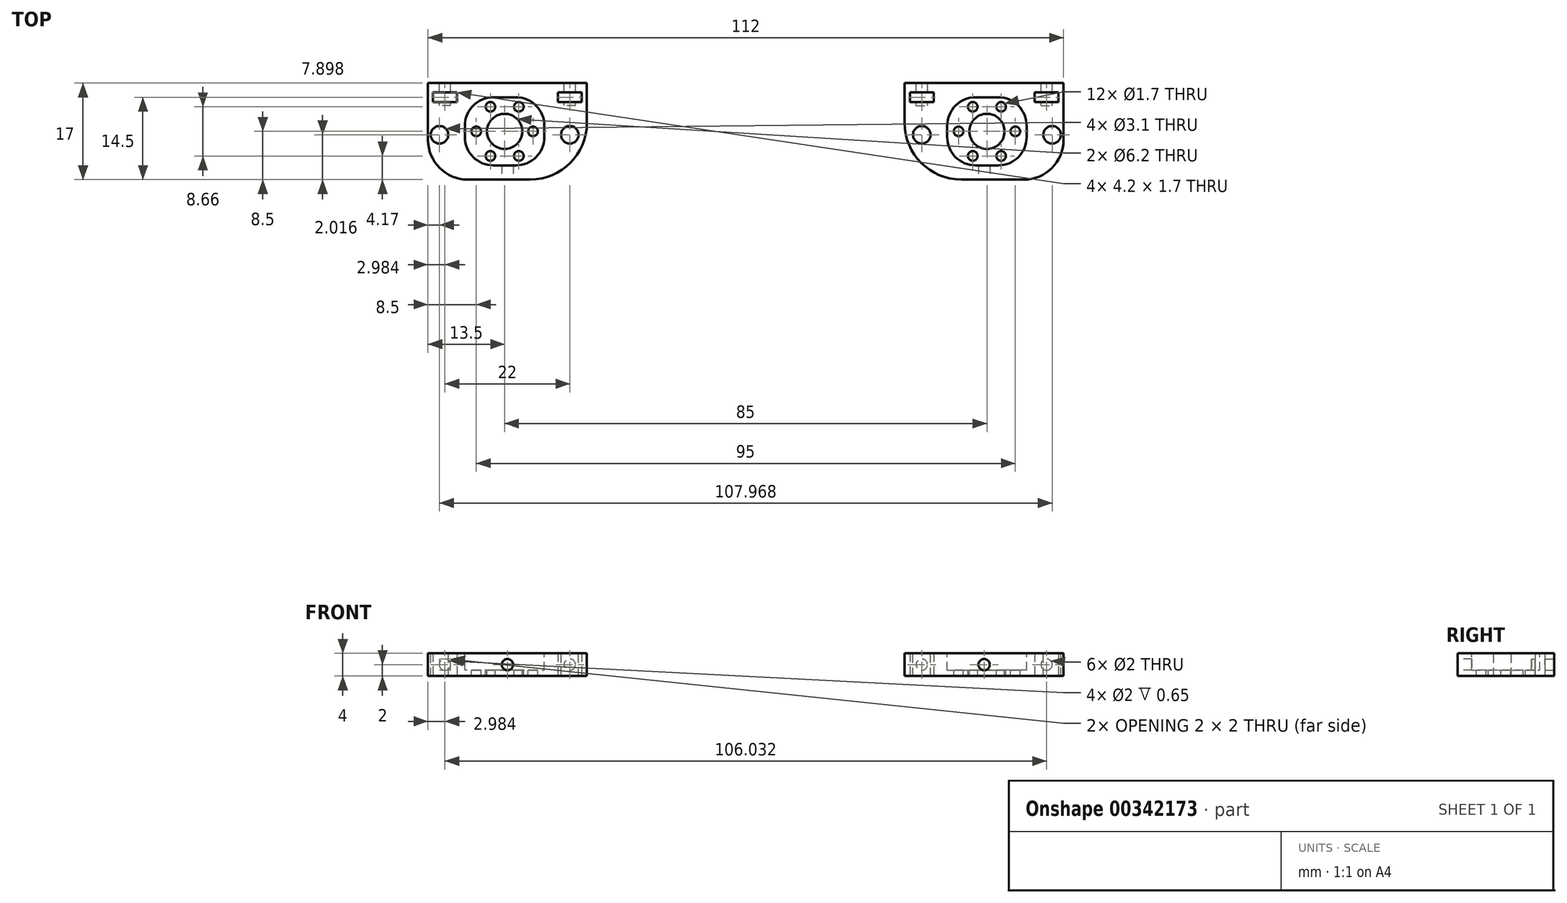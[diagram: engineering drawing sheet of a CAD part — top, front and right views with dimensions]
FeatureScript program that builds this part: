
annotation { "Feature Type Name" : "Feature", "Feature Type Description" : "" }
export const myFeature = defineFeature(function(context is Context, id is Id, definition is map)
    precondition{}
    {
        {
            var Q0;
            Q0=qCreatedBy(makeId("Front.planeOp"),FACE);
            var sketch = newSketch(context, id + "F0", { "sketchPlane" : qUnion([Q0])});
            skLineSegment(sketch, "E0.bottom", {"start": v(0, 0) * mm, "end": v(28, 0) * mm});
            skLineSegment(sketch, "E0.top", {"start": v(0, 17) * mm, "end": v(28, 17) * mm});
            skLineSegment(sketch, "E0.left", {"start": v(0, 0) * mm, "end": v(0, 17) * mm});
            skLineSegment(sketch, "E0.right", {"start": v(28, 0) * mm, "end": v(28, 17) * mm});
            skCircle(sketch, "E1", {"center": v(14.5, 8.5) * mm, "radius": 3.1 * mm});
            skCircle(sketch, "E2", {"center": v(19.5, 8.5) * mm, "radius": 0.85 * mm});
            skCircle(sketch, "E3.1.0", {"center": v(17, 12.83) * mm, "radius": 0.85 * mm});
            skCircle(sketch, "E3.2.0", {"center": v(12, 12.83) * mm, "radius": 0.85 * mm});
            skCircle(sketch, "E3.3.0", {"center": v(9.5, 8.5) * mm, "radius": 0.85 * mm});
            skCircle(sketch, "E3.4.0", {"center": v(12, 4.17) * mm, "radius": 0.85 * mm});
            skCircle(sketch, "E3.5.0", {"center": v(17, 4.17) * mm, "radius": 0.85 * mm});
            skLineSegment(sketch, "E4.bottom", {"start": v(7.5, 14.5) * mm, "end": v(21.5, 14.5) * mm});
            skLineSegment(sketch, "E4.top", {"start": v(7.5, 2.5) * mm, "end": v(21.5, 2.5) * mm});
            skLineSegment(sketch, "E4.left", {"start": v(7.5, 14.5) * mm, "end": v(7.5, 2.5) * mm});
            skLineSegment(sketch, "E4.right", {"start": v(21.5, 14.5) * mm, "end": v(21.5, 2.5) * mm});
            skCircle(sketch, "E5", {"center": v(3.02, 9.1) * mm, "radius": 1.55 * mm});
            skLineSegment(sketch, "E6", {"start": v(3.02, 9.1) * mm, "end": v(14.5, 8.5) * mm});
            skLineSegment(sketch, "E7", {"start": v(14.5, 8.5) * mm, "end": v(0, 8.5) * mm});
            skLineSegment(sketch, "E8", {"start": v(14.5, 8.5) * mm, "end": v(14.5, 11.6) * mm});
            skCircle(sketch, "E9.MirrorC", {"center": v(25.98, 9.1) * mm, "radius": 1.55 * mm});
            skSolve(sketch);
        }
        {
            var Q0;
            Q0=makeQuery(id+"F0.imprint","IMPRINT",FACE,{"disambiguationData":[TD([[makeQuery(id+"F0.imprint","IMPRINT",EDGE,{"derivedFrom":sQuery(id+"F0.wireOp",EDGE,"E0.bottom")}),1.0]])]});
            var Q1;
            Q1=makeQuery(id+"F0.imprint","IMPRINT",FACE,{"disambiguationData":[TD([[makeQuery(id+"F0.imprint","IMPRINT",EDGE,{"derivedFrom":sQuery(id+"F0.wireOp",EDGE,"E1")}),-1.0]])]});
            var Q2;
            Q2=makeQuery(id+"F0.imprint","IMPRINT",FACE,{"disambiguationData":[TD([[makeQuery(id+"F0.imprint","IMPRINT",EDGE,{"derivedFrom":sQuery(id+"F0.wireOp",EDGE,"E2")}),-1.0]])]});
            var Q3;
            {var subQ0=sQuery(id+"F0.wireOp",EDGE,"E6");var subQ1=sQuery(id+"F0.wireOp",EDGE,"E3.3.0");var subQ2=makeQuery(id+"F0.imprint","INTERSECT",VERTEX,{"disambiguationData":[OD(0.0)],"derivedFrom":[subQ1,subQ0]});Q3=makeQuery(id+"F0.imprint","IMPRINT",FACE,{"disambiguationData":[TD([[makeQuery(id+"F0.imprint","IMPRINT",EDGE,{"disambiguationData":[TD([[subQ2,1.0]])],"derivedFrom":subQ1}),-1.0]])]});}
            var Q4;
            {var subQ0=sQuery(id+"F0.wireOp",EDGE,"E7");var subQ1=sQuery(id+"F0.wireOp",EDGE,"E4.left");var subQ2=makeQuery(id+"F0.imprint","INTERSECT",VERTEX,{"derivedFrom":[subQ1,subQ0]});Q4=makeQuery(id+"F0.imprint","IMPRINT",FACE,{"disambiguationData":[TD([[makeQuery(id+"F0.imprint","IMPRINT",EDGE,{"disambiguationData":[TD([[subQ2,-1.0]])],"derivedFrom":subQ1}),-1.0]])]});}
            var Q5;
            {var subQ0=sQuery(id+"F0.wireOp",EDGE,"E6");var subQ1=sQuery(id+"F0.wireOp",EDGE,"E4.left");var subQ2=makeQuery(id+"F0.imprint","INTERSECT",VERTEX,{"derivedFrom":[subQ1,subQ0]});Q5=makeQuery(id+"F0.imprint","IMPRINT",FACE,{"disambiguationData":[TD([[makeQuery(id+"F0.imprint","IMPRINT",EDGE,{"disambiguationData":[TD([[subQ2,-1.0]])],"derivedFrom":subQ1}),-1.0]])]});}
            var Q6;
            {var subQ0=sQuery(id+"F0.wireOp",EDGE,"E6");var subQ1=sQuery(id+"F0.wireOp",EDGE,"E3.3.0");var subQ2=makeQuery(id+"F0.imprint","INTERSECT",VERTEX,{"disambiguationData":[OD(1.0)],"derivedFrom":[subQ1,subQ0]});Q6=makeQuery(id+"F0.imprint","IMPRINT",FACE,{"disambiguationData":[TD([[makeQuery(id+"F0.imprint","IMPRINT",EDGE,{"disambiguationData":[TD([[subQ2,-1.0]])],"derivedFrom":subQ1}),-1.0]])]});}
            extrude(context, id + "F1", {"entities" : qUnion([Q0, Q1, Q2, Q3, Q4, Q5, Q6]), "depth" : 4 * mm});
        }
        {
            var Q0;
            Q0=makeQuery(id+"F1.opExtrude","SWEPT_EDGE",EDGE,{"disambiguationData":[OSD([sQuery(id+"F0.wireOp",EDGE,"E0.top"),sQuery(id+"F0.wireOp",EDGE,"E0.left")])]});
            fillet(context, id + "F2", {"entities" : qUnion([Q0]), "radius" : 10 * mm, "tangentPropagation" : true, "allowEdgeOverflow" : false});
        }
        {
            var Q0;
            Q0=makeQuery(id+"F0.imprint","IMPRINT",FACE,{"disambiguationData":[TD([[makeQuery(id+"F0.imprint","IMPRINT",EDGE,{"derivedFrom":sQuery(id+"F0.wireOp",EDGE,"E2")}),-1.0]])]});
            var Q1;
            {var subQ0=sQuery(id+"F0.wireOp",EDGE,"E6");var subQ1=sQuery(id+"F0.wireOp",EDGE,"E1");var subQ2=makeQuery(id+"F0.imprint","INTERSECT",VERTEX,{"derivedFrom":[subQ1,subQ0]});Q1=makeQuery(id+"F0.imprint","IMPRINT",FACE,{"disambiguationData":[TD([[makeQuery(id+"F0.imprint","IMPRINT",EDGE,{"disambiguationData":[TD([[subQ2,1.0]])],"derivedFrom":subQ1}),-1.0]])]});}
            var Q2;
            {var subQ0=sQuery(id+"F0.wireOp",EDGE,"E6");var subQ1=sQuery(id+"F0.wireOp",EDGE,"E3.3.0");var subQ2=makeQuery(id+"F0.imprint","INTERSECT",VERTEX,{"disambiguationData":[OD(1.0)],"derivedFrom":[subQ1,subQ0]});Q2=makeQuery(id+"F0.imprint","IMPRINT",FACE,{"disambiguationData":[TD([[makeQuery(id+"F0.imprint","IMPRINT",EDGE,{"disambiguationData":[TD([[subQ2,-1.0]])],"derivedFrom":subQ1}),-1.0]])]});}
            var Q3;
            {var subQ0=sQuery(id+"F0.wireOp",EDGE,"E6");var subQ1=sQuery(id+"F0.wireOp",EDGE,"E1");var subQ2=makeQuery(id+"F0.imprint","INTERSECT",VERTEX,{"derivedFrom":[subQ1,subQ0]});Q3=makeQuery(id+"F0.imprint","IMPRINT",FACE,{"disambiguationData":[TD([[makeQuery(id+"F0.imprint","IMPRINT",EDGE,{"disambiguationData":[TD([[subQ2,-1.0]])],"derivedFrom":subQ1}),-1.0]])]});}
            extrude(context, id + "F3", {"entities" : qUnion([Q0, Q1, Q2, Q3]), "operationType" : NewBodyOperationType.REMOVE, "depth" : 3 * mm});
        }
        {
            var Q0;
            Q0=makeQuery(id+"F3.boolean.opBoolean","COPY",EDGE,{"derivedFrom":makeQuery(id+"F3.opExtrude","SWEPT_EDGE",EDGE,{"disambiguationData":[OSD([sQuery(id+"F0.wireOp",EDGE,"E4.bottom"),sQuery(id+"F0.wireOp",EDGE,"E4.right")])]})});
            var Q1;
            Q1=makeQuery(id+"F3.boolean.opBoolean","COPY",EDGE,{"derivedFrom":makeQuery(id+"F3.opExtrude","SWEPT_EDGE",EDGE,{"disambiguationData":[OSD([sQuery(id+"F0.wireOp",EDGE,"E4.top"),sQuery(id+"F0.wireOp",EDGE,"E4.right")])]})});
            var Q2;
            Q2=makeQuery(id+"F3.boolean.opBoolean","COPY",EDGE,{"derivedFrom":makeQuery(id+"F3.opExtrude","SWEPT_EDGE",EDGE,{"disambiguationData":[OSD([sQuery(id+"F0.wireOp",EDGE,"E4.top"),sQuery(id+"F0.wireOp",EDGE,"E4.left")])]})});
            var Q3;
            Q3=makeQuery(id+"F3.boolean.opBoolean","COPY",EDGE,{"derivedFrom":makeQuery(id+"F3.opExtrude","SWEPT_EDGE",EDGE,{"disambiguationData":[OSD([sQuery(id+"F0.wireOp",EDGE,"E4.bottom"),sQuery(id+"F0.wireOp",EDGE,"E4.left")])]})});
            fillet(context, id + "F4", {"entities" : qUnion([Q0, Q1, Q2, Q3]), "radius" : 5 * mm, "tangentPropagation" : true, "allowEdgeOverflow" : false});
        }
        {
            var Q0;
            Q0=makeQuery(id+"F1.opExtrude","SWEPT_EDGE",EDGE,{"disambiguationData":[OSD([sQuery(id+"F0.wireOp",EDGE,"E0.top"),sQuery(id+"F0.wireOp",EDGE,"E0.right")])]});
            fillet(context, id + "F5", {"entities" : qUnion([Q0]), "radius" : 7 * mm, "tangentPropagation" : true, "allowEdgeOverflow" : false});
        }
        {
            var Q0;
            Q0=makeQuery(id+"F1.opExtrude","SWEPT_FACE",FACE,{"disambiguationData":[OSD([sQuery(id+"F0.wireOp",EDGE,"E0.bottom")])]});
            var sketch = newSketch(context, id + "F6", { "sketchPlane" : qUnion([Q0])});
            skCircle(sketch, "E10", {"center": v(3.02, 2) * mm, "radius": 1 * mm});
            skCircle(sketch, "E11", {"center": v(25.02, 2) * mm, "radius": 1 * mm});
            skSolve(sketch);
        }
        {
            var Q0;
            Q0=qSketchRegion(id+"F6",true);
            extrude(context, id + "F7", {"entities" : qUnion([Q0]), "operationType" : NewBodyOperationType.REMOVE, "oppositeDirection" : true, "depth" : 4 * mm});
        }
        {
            var Q0;
            Q0=makeQuery(id+"F1.opExtrude","CAP_FACE",FACE,{"disambiguationData":[OSD([sQuery(id+"F0.wireOp",EDGE,"E0.bottom"),sQuery(id+"F0.wireOp",EDGE,"E0.top"),sQuery(id+"F0.wireOp",EDGE,"E0.left"),sQuery(id+"F0.wireOp",EDGE,"E0.right"),sQuery(id+"F0.wireOp",EDGE,"wE7doQa1-f1d0-D7SE-Vx9v-5G1ykLdNQw0D"),sQuery(id+"F0.wireOp",EDGE,"E1"),sQuery(id+"F0.wireOp",EDGE,"E2"),sQuery(id+"F0.wireOp",EDGE,"E3.1.0"),sQuery(id+"F0.wireOp",EDGE,"E3.2.0"),sQuery(id+"F0.wireOp",EDGE,"E3.3.0"),sQuery(id+"F0.wireOp",EDGE,"E3.4.0"),sQuery(id+"F0.wireOp",EDGE,"E3.5.0")])],"isStart":false});
            var sketch = newSketch(context, id + "F8", { "sketchPlane" : qUnion([Q0])});
            skLineSegment(sketch, "E12.bottom", {"start": v(0.92, 3.35) * mm, "end": v(5.12, 3.35) * mm});
            skLineSegment(sketch, "E12.top", {"start": v(0.92, 1.65) * mm, "end": v(5.12, 1.65) * mm});
            skLineSegment(sketch, "E12.left", {"start": v(0.92, 3.35) * mm, "end": v(0.92, 1.65) * mm});
            skLineSegment(sketch, "E12.right", {"start": v(5.12, 3.35) * mm, "end": v(5.12, 1.65) * mm});
            skPoint(sketch, "E12.middle", {"position": v(3.02, 2.5) * mm});
            skLineSegment(sketch, "E13.bottom", {"start": v(27.12, 3.35) * mm, "end": v(22.92, 3.35) * mm});
            skLineSegment(sketch, "E13.top", {"start": v(27.12, 1.65) * mm, "end": v(22.92, 1.65) * mm});
            skLineSegment(sketch, "E13.left", {"start": v(27.12, 3.35) * mm, "end": v(27.12, 1.65) * mm});
            skLineSegment(sketch, "E13.right", {"start": v(22.92, 3.35) * mm, "end": v(22.92, 1.65) * mm});
            skPoint(sketch, "E13.middle", {"position": v(25.02, 2.5) * mm});
            skSolve(sketch);
        }
        {
            var Q0;
            Q0=qSketchRegion(id+"F8",true);
            extrude(context, id + "F9", {"entities" : qUnion([Q0]), "operationType" : NewBodyOperationType.REMOVE, "oppositeDirection" : true, "depth" : 4 * mm});
        }
        {
            var Q0;
            Q0=makeQuery(id+"F1.opExtrude","SWEPT_FACE",FACE,{"disambiguationData":[OSD([sQuery(id+"F0.wireOp",EDGE,"E0.top")])]});
            var sketch = newSketch(context, id + "F10", { "sketchPlane" : qUnion([Q0])});
            skPoint(sketch, "E14", {"position": v(15.5, -4) * mm});
            skPoint(sketch, "E15.positionSnap0", {"position": v(10, -2) * mm});
            skPoint(sketch, "E16", {"position": v(0, -2) * mm});
            skPoint(sketch, "E17", {"position": v(14, -2) * mm});
            skCircle(sketch, "E18", {"center": v(14, -2) * mm, "radius": 1 * mm});
            skSolve(sketch);
        }
        {
            var Q0;
            Q0=makeQuery(id+"F10.imprint","IMPRINT",FACE,{"disambiguationData":[TD([[makeQuery(id+"F10.imprint","IMPRINT",EDGE,{"derivedFrom":sQuery(id+"F10.wireOp",EDGE,"E18")}),1.0]])]});
            extrude(context, id + "F11", {"entities" : qUnion([Q0]), "operationType" : NewBodyOperationType.REMOVE, "oppositeDirection" : true, "depth" : 8 * mm});
        }
        {
            var Q0;
            Q0=makeQuery(id+"F1.opExtrude","SWEPT_BODY",BODY,{"disambiguationData":[OSD([sQuery(id+"F0.wireOp",EDGE,"E0.bottom"),sQuery(id+"F0.wireOp",EDGE,"E0.top"),sQuery(id+"F0.wireOp",EDGE,"E0.left"),sQuery(id+"F0.wireOp",EDGE,"E0.right"),sQuery(id+"F0.wireOp",EDGE,"E1"),sQuery(id+"F0.wireOp",EDGE,"E2"),sQuery(id+"F0.wireOp",EDGE,"E3.1.0"),sQuery(id+"F0.wireOp",EDGE,"E3.2.0"),sQuery(id+"F0.wireOp",EDGE,"E3.3.0"),sQuery(id+"F0.wireOp",EDGE,"E3.4.0"),sQuery(id+"F0.wireOp",EDGE,"E3.5.0"),sQuery(id+"F0.wireOp",EDGE,"E5"),sQuery(id+"F0.wireOp",EDGE,"9a4bb128-1836-41c6-8c04-a79236455e590.MirrorC")])]});
            var Q1;
            Q1=sQuery(id+"F0.wireOp",EDGE,"E0.bottom");
            transform(context, id + "F12", {"entities" : qUnion([Q0]), "transformType" : TransformType.TRANSLATION_ENTITY, "oppositeDirectionEntity" : false, "transformLine" : qUnion([Q1]), "makeCopy" : false});
        }
        {
            var Q0;
            Q0=makeQuery(id+"F1.opExtrude","SWEPT_BODY",BODY,{"disambiguationData":[OSD([sQuery(id+"F0.wireOp",EDGE,"E0.bottom"),sQuery(id+"F0.wireOp",EDGE,"E0.top"),sQuery(id+"F0.wireOp",EDGE,"E0.left"),sQuery(id+"F0.wireOp",EDGE,"E0.right"),sQuery(id+"F0.wireOp",EDGE,"E1"),sQuery(id+"F0.wireOp",EDGE,"E2"),sQuery(id+"F0.wireOp",EDGE,"E3.1.0"),sQuery(id+"F0.wireOp",EDGE,"E3.2.0"),sQuery(id+"F0.wireOp",EDGE,"E3.3.0"),sQuery(id+"F0.wireOp",EDGE,"E3.4.0"),sQuery(id+"F0.wireOp",EDGE,"E3.5.0"),sQuery(id+"F0.wireOp",EDGE,"E5"),sQuery(id+"F0.wireOp",EDGE,"9a4bb128-1836-41c6-8c04-a79236455e590.MirrorC")])]});
            var Q1;
            Q1=sQuery(id+"F0.wireOp",EDGE,"E0.bottom");
            transform(context, id + "F13", {"entities" : qUnion([Q0]), "transformType" : TransformType.ROTATION, "transformAxis" : qUnion([Q1]), "angle" : 90 * degree, "makeCopy" : false});
        }
        {
            var Q0;
            Q0=makeQuery(id+"F1.opExtrude","SWEPT_BODY",BODY,{"disambiguationData":[OSD([sQuery(id+"F0.wireOp",EDGE,"E0.bottom"),sQuery(id+"F0.wireOp",EDGE,"E0.top"),sQuery(id+"F0.wireOp",EDGE,"E0.left"),sQuery(id+"F0.wireOp",EDGE,"E0.right"),sQuery(id+"F0.wireOp",EDGE,"E1"),sQuery(id+"F0.wireOp",EDGE,"E2"),sQuery(id+"F0.wireOp",EDGE,"E3.1.0"),sQuery(id+"F0.wireOp",EDGE,"E3.2.0"),sQuery(id+"F0.wireOp",EDGE,"E3.3.0"),sQuery(id+"F0.wireOp",EDGE,"E3.4.0"),sQuery(id+"F0.wireOp",EDGE,"E3.5.0"),sQuery(id+"F0.wireOp",EDGE,"E5"),sQuery(id+"F0.wireOp",EDGE,"9a4bb128-1836-41c6-8c04-a79236455e590.MirrorC")])]});
            var Q1;
            Q1=qCreatedBy(makeId("Right.planeOp"),FACE);
            mirror(context, id + "F14", {"entities" : qUnion([Q0]), "mirrorPlane" : qUnion([Q1])});
        }
    });
